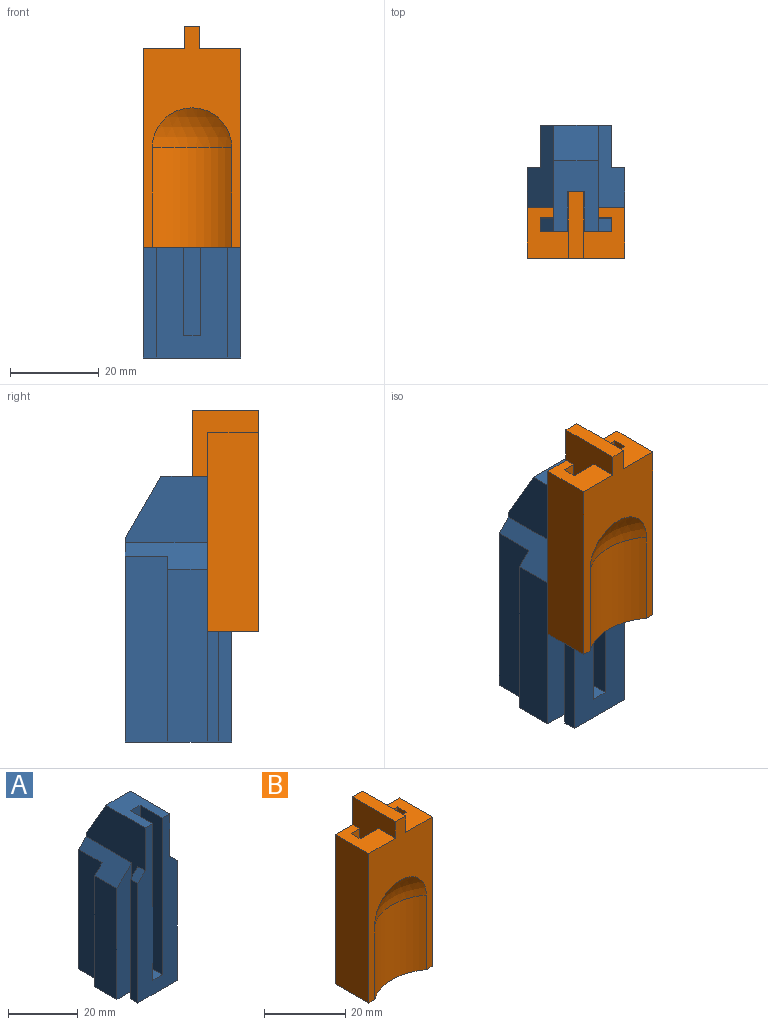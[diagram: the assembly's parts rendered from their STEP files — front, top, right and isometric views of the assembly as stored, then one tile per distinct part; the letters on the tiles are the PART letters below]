
ASSEMBLY  parts=2 mates=1
PART A: 34 faces, bbox 22x24x60 mm
  f0: plane 42x3mm, normal (1,0,0), area 126mm2, adj f1,f2,f6,f27
  f1: plane 3x3mm, normal (0.71,0,0.71), area 12.7mm2, adj f0,f6,f16,f27
  f2: plane 24x22mm, normal (0,0,-1), area 390.8mm2, adj f0,f3,f6,f7,f8,f9,f14,f16
  f3: plane 42x3mm, normal (-1,0,0), area 126mm2, adj f2,f6,f15,f26
  f4: plane 18.5x6mm, normal (-0.71,0,0.71), area 116.7mm2, adj f7,f9,f14,f25,f32,f33
  f5: plane 16x10mm, normal (0,0,1), area 126.2mm2, adj f6,f10,f12,f13,f14,f16,f29
  f6: plane 60x16mm, normal (0,-1,0), area 654.8mm2, adj f0,f1,f2,f3,f5,f10,f11,f12
  f7: plane 46.14x16mm, normal (0,1,0), area 722.4mm2, adj f2,f4,f8,f9,f14,f16,f17,f29
  f8: plane 42x9.5mm, normal (1,0,0), area 399mm2, adj f2,f7,f17,f30
  f9: plane 42x9.5mm, normal (-1,0,0), area 399mm2, adj f2,f4,f7,f32
  f10: plane 55x9mm, normal (1,0,0), area 495mm2, adj f5,f6,f11,f13
  f11: plane 9x3.75mm, normal (0,0,1), area 33.7mm2, adj f6,f10,f12,f13
  f12: plane 55x9mm, normal (-1,0,0), area 495mm2, adj f5,f6,f11,f13
  f13: plane 55x3.75mm, normal (0,-1,0), area 206.2mm2, adj f5,f10,f11,f12
  f14: plane 60x24mm, normal (-1,0,0), area 417.1mm2, adj f2,f4,f5,f6,f7,f15,f25,f26
  f15: plane 3x3mm, normal (-0.71,0,0.71), area 12.7mm2, adj f3,f6,f14,f26
  f16: plane 60x24mm, normal (1,0,0), area 417.1mm2, adj f1,f2,f5,f6,f7,f17,f27,f28
  f17: plane 18.5x6mm, normal (0.71,0,0.71), area 116.7mm2, adj f7,f8,f16,f28,f30,f31
  f18: plane 24x3.52mm, normal (0,-1,0), area 84.5mm2, adj f2,f19,f23,f24
  f19: plane 24x3.05mm, normal (-0.87,-0.5,0), area 84.5mm2, adj f2,f18,f20,f24
  f20: plane 24x3.05mm, normal (-0.87,0.5,0), area 84.5mm2, adj f2,f19,f21,f24
  f21: plane 24x3.52mm, normal (0,1,0), area 84.5mm2, adj f2,f20,f22,f24
  f22: plane 24x3.05mm, normal (0.87,0.5,0), area 84.5mm2, adj f2,f21,f23,f24
  f23: plane 24x3.05mm, normal (0.87,-0.5,0), area 84.5mm2, adj f2,f18,f22,f24
  f24: plane 7.04x6.1mm, normal (0,0,-1), area 32.2mm2, adj f18,f19,f20,f21,f22,f23
  f25: plane 45x6mm, normal (0,-1,0), area 252mm2, adj f2,f4,f14,f33
  f26: plane 45x3mm, normal (0,1,0), area 130.5mm2, adj f2,f3,f14,f15
  f27: plane 45x3mm, normal (0,1,0), area 130.5mm2, adj f0,f1,f2,f16
  f28: plane 45x6mm, normal (0,-1,0), area 252mm2, adj f2,f16,f17,f31
  f29: plane 13.86x10mm, normal (0,0.87,0.5), area 160mm2, adj f5,f7,f14,f16
  f30: plane 42x3mm, normal (0,1,0), area 121.5mm2, adj f2,f8,f17,f31
  f31: plane 39x9mm, normal (1,0,0), area 351mm2, adj f2,f17,f28,f30
  f32: plane 42x3mm, normal (0,1,0), area 121.5mm2, adj f2,f4,f9,f33
  f33: plane 39x9mm, normal (-1,0,0), area 351mm2, adj f2,f4,f25,f32
PART B: 22 faces, bbox 22.1x17.4x50 mm
  f0: plane 22.13x11.5mm, normal (0,0,-1), area 143.2mm2, adj f3,f4,f5,f6,f7,f8,f9,f10
  f1: sphere r=15mm, area 141.4mm2, adj f20,f21
  f2: plane 11.5x9.31mm, normal (0,0,1), area 79.5mm2, adj f3,f4,f5,f6,f12,f13,f17,f20
  f3: plane 45x3mm, normal (0,-1,0), area 135mm2, adj f0,f2,f4,f13
  f4: plane 45x2.38mm, normal (1,0,0), area 106.9mm2, adj f0,f2,f3,f5
  f5: plane 45x6mm, normal (0,1,0), area 270mm2, adj f0,f2,f4,f6
  f6: plane 45x11.5mm, normal (-1,0,0), area 517.5mm2, adj f0,f2,f5,f20
  f7: plane 45x11.5mm, normal (1,0,0), area 517.5mm2, adj f0,f8,f14,f20
  f8: plane 45x6mm, normal (0,1,0), area 270mm2, adj f0,f7,f9,f14
  f9: plane 45x2.38mm, normal (-1,0,0), area 106.9mm2, adj f0,f8,f10,f14
  f10: plane 45x3mm, normal (0,-1,0), area 135mm2, adj f0,f9,f11,f14
  f11: plane 45x3.13mm, normal (-1,0,0), area 140.6mm2, adj f0,f10,f12,f14
  f12: plane 45x16.13mm, normal (0,1,0), area 585.6mm2, adj f0,f2,f11,f13,f14,f15,f16,f17
  f13: plane 45x3.13mm, normal (1,0,0), area 140.6mm2, adj f0,f2,f3,f12
  f14: plane 11.5x9.31mm, normal (0,0,1), area 79.5mm2, adj f7,f8,f9,f10,f11,f12,f15,f20
  f15: plane 45x15mm, normal (1,0,0), area 435mm2, adj f12,f14,f16,f18,f19,f20
  f16: plane 9x3.5mm, normal (0,0,-1), area 31.5mm2, adj f12,f15,f17,f19
  f17: plane 45x15mm, normal (-1,0,0), area 435mm2, adj f2,f12,f16,f18,f19,f20
  f18: plane 15x3.5mm, normal (0,0,1), area 52.5mm2, adj f15,f17,f19,f20
  f19: plane 45x3.5mm, normal (0,1,0), area 157.5mm2, adj f15,f16,f17,f18
  f20: plane 50x22.13mm, normal (0,-1,0), area 480.9mm2, adj f0,f1,f2,f6,f7,f14,f15,f17
  f21: cylinder r=15mm len=22.5mm, axis (0,0,-1), area 434.4mm2, adj f0,f1,f20
PLACE A t=(-0.09,0.12,-6.53)mm fixed
PLACE B t=(-0.09,-11.95,10.97)mm
MATE slider B.f16 <-> A.f11  axis (0,0,-1) through (-0.09,-11.88,-6.53)mm
